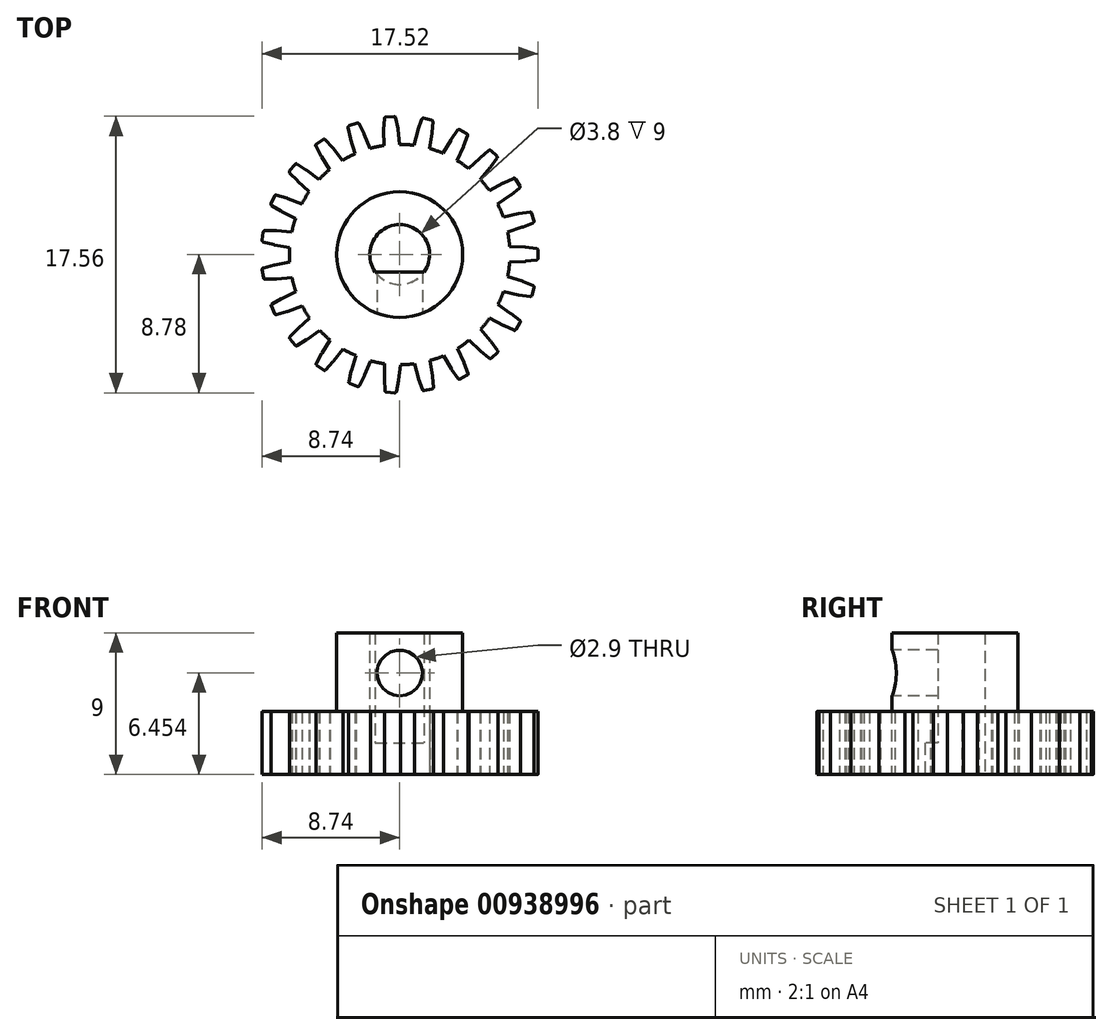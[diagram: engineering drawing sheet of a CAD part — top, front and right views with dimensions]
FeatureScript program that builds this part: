
annotation { "Feature Type Name" : "Feature", "Feature Type Description" : "" }
export const myFeature = defineFeature(function(context is Context, id is Id, definition is map)
    precondition{}
    {
        {
            var Q0;
            Q0=qCreatedBy(makeId("Top.planeOp"),FACE);
            var sketch = newSketch(context, id + "F0", { "sketchPlane" : qUnion([Q0])});
            skArc(sketch, "E0", {"start": v(-1, 6.93) * mm, "mid": v(0.5, -6.98) * mm, "end": v(0, 7) * mm});
            skCircle(sketch, "E1", {"center": v(0, 0) * mm, "radius": 4 * mm});
            skLineSegment(sketch, "E2", {"start": v(-1, 6.93) * mm, "end": v(0, 7) * mm});
            skCircle(sketch, "E3", {"center": v(0, 0) * mm, "radius": 1.9 * mm});
            skLineSegment(sketch, "E4", {"start": v(-0.5, 6.96) * mm, "end": v(-0.57, 7.96) * mm});
            skLineSegment(sketch, "E5", {"start": v(-0.57, 7.96) * mm, "end": v(-1.01, 7.93) * mm});
            skLineSegment(sketch, "E6", {"start": v(-1.01, 7.93) * mm, "end": v(-0.12, 8) * mm});
            skLineSegment(sketch, "E7", {"start": v(-1.01, 7.91) * mm, "end": v(-1, 6.93) * mm});
            skLineSegment(sketch, "E8", {"start": v(-0.11, 7.97) * mm, "end": v(0, 7) * mm});
            skLineSegment(sketch, "E9", {"start": v(-0.57, 7.96) * mm, "end": v(-0.62, 8.76) * mm});
            skLineSegment(sketch, "E10", {"start": v(-0.62, 8.76) * mm, "end": v(-0.88, 8.74) * mm});
            skLineSegment(sketch, "E11", {"start": v(-0.88, 8.74) * mm, "end": v(-0.36, 8.78) * mm});
            skLineSegment(sketch, "E12", {"start": v(-0.97, 8.65) * mm, "end": v(-1.01, 7.95) * mm});
            skLineSegment(sketch, "E13", {"start": v(-0.25, 8.7) * mm, "end": v(-0.12, 8) * mm});
            skPoint(sketch, "E14.visualSharp", {"position": v(-0.27, 8.78) * mm});
            skArc(sketch, "E14.filletArc", {"start": v(-0.25, 8.7) * mm, "mid": v(-0.3, 8.76) * mm, "end": v(-0.36, 8.78) * mm});
            skPoint(sketch, "E15.visualSharp", {"position": v(-0.97, 8.73) * mm});
            skArc(sketch, "E15.filletArc", {"start": v(-0.88, 8.74) * mm, "mid": v(-0.94, 8.71) * mm, "end": v(-0.97, 8.65) * mm});
            skPoint(sketch, "E16.visualSharp", {"position": v(-0.12, 8) * mm});
            skArc(sketch, "E16.filletArc", {"start": v(-0.11, 7.97) * mm, "mid": v(-0.12, 8) * mm, "end": v(-0.12, 8) * mm});
            skPoint(sketch, "E17.visualSharp", {"position": v(-1.01, 7.93) * mm});
            skArc(sketch, "E17.filletArc", {"start": v(-1.01, 7.95) * mm, "mid": v(-1.01, 7.93) * mm, "end": v(-1.01, 7.91) * mm});
            skLineSegment(sketch, "E18", {"start": v(0, 1.9) * mm, "end": v(0, -1.1) * mm, "construction": true});
            skLineSegment(sketch, "E19", {"start": v(-1.55, -1.1) * mm, "end": v(1.55, -1.1) * mm});
            skSolve(sketch);
        }
        {
            var Q0;
            Q0=qCreatedBy(makeId("Front.planeOp"),FACE);
            var sketch = newSketch(context, id + "F1", { "sketchPlane" : qUnion([Q0])});
            skLineSegment(sketch, "E20", {"start": v(0, 0) * mm, "end": v(0, 26.77) * mm, "construction": true});
            skSolve(sketch);
        }
        {
            var Q0;
            Q0=makeQuery(id+"F0.imprint","IMPRINT",FACE,{"disambiguationData":[TD([[makeQuery(id+"F0.imprint","IMPRINT",EDGE,{"derivedFrom":sQuery(id+"F0.wireOp",EDGE,"E1")}),1.0]])]});
            var Q1;
            {var subQ0=sQuery(id+"F0.wireOp",EDGE,"E19");Q1=makeQuery(id+"F0.imprint","IMPRINT",FACE,{"disambiguationData":[TD([[makeQuery(id+"F0.imprint","IMPRINT",EDGE,{"derivedFrom":subQ0}),-1.0]])]});}
            extrude(context, id + "F2", {"entities" : qUnion([Q0, Q1]), "depth" : 7 * mm, "offsetDistance" : 25 * mm});
        }
        {
            var Q0;
            Q0=makeQuery(id+"F0.imprint","IMPRINT",FACE,{"disambiguationData":[TD([[makeQuery(id+"F0.imprint","IMPRINT",EDGE,{"derivedFrom":sQuery(id+"F0.wireOp",EDGE,"E1")}),1.0]])]});
            extrude(context, id + "F3", {"entities" : qUnion([Q0]), "operationType" : NewBodyOperationType.ADD, "oppositeDirection" : true, "depth" : 2 * mm, "offsetDistance" : 25 * mm});
        }
        {
            var Q0;
            Q0=makeQuery(id+"F0.imprint","IMPRINT",FACE,{"disambiguationData":[TD([[makeQuery(id+"F0.imprint","IMPRINT",EDGE,{"derivedFrom":sQuery(id+"F0.wireOp",EDGE,"E1")}),-1.0]])]});
            extrude(context, id + "F4", {"entities" : qUnion([Q0]), "operationType" : NewBodyOperationType.ADD, "depth" : 4 * mm, "offsetDistance" : 25 * mm, "symmetric" : true});
        }
        {
            var Q0;
            Q0=makeQuery(id+"F0.imprint","IMPRINT",FACE,{"disambiguationData":[TD([[makeQuery(id+"F0.imprint","IMPRINT",EDGE,{"derivedFrom":sQuery(id+"F0.wireOp",EDGE,"E2")}),1.0]])]});
            var Q1;
            {var subQ0=sQuery(id+"F0.wireOp",EDGE,"185f444b-8d71-4d4d-b295-205664a3cbeb");Q1=makeQuery(id+"F0.imprint","IMPRINT",FACE,{"disambiguationData":[TD([[makeQuery(id+"F0.imprint","IMPRINT",EDGE,{"derivedFrom":subQ0}),1.0]])]});}
            var Q2;
            {var subQ0=sQuery(id+"F0.wireOp",EDGE,"185f444b-8d71-4d4d-b295-205664a3cbeb");Q2=makeQuery(id+"F0.imprint","IMPRINT",FACE,{"disambiguationData":[TD([[makeQuery(id+"F0.imprint","IMPRINT",EDGE,{"derivedFrom":subQ0}),-1.0]])]});}
            var Q3;
            {var subQ1=sQuery(id+"F0.wireOp",EDGE,"E9");Q3=makeQuery(id+"F0.imprint","IMPRINT",FACE,{"disambiguationData":[TD([[makeQuery(id+"F0.imprint","IMPRINT",EDGE,{"derivedFrom":subQ1}),1.0]])]});}
            var Q4;
            {var subQ1=sQuery(id+"F0.wireOp",EDGE,"E9");Q4=makeQuery(id+"F0.imprint","IMPRINT",FACE,{"disambiguationData":[TD([[makeQuery(id+"F0.imprint","IMPRINT",EDGE,{"derivedFrom":subQ1}),-1.0]])]});}
            extrude(context, id + "F5", {"entities" : qUnion([Q0, Q1, Q2, Q3, Q4]), "depth" : 4 * mm, "offsetDistance" : 25 * mm, "symmetric" : true});
        }
        {
            var Q0;
            Q0=makeQuery(id+"F5.opExtrude","SWEPT_BODY",BODY,{"disambiguationData":[OSD([sQuery(id+"F0.wireOp",EDGE,"E2"),sQuery(id+"F0.wireOp",EDGE,"zY2qvlCe-LwUi-iNXd-wZ7Z-H6Lx6uWpxhC7"),sQuery(id+"F0.wireOp",EDGE,"CL1w9jXF-FcO4-JGJ7-eMMN-SI9SSlm3FFuX")])]});
            var Q1;
            Q1=sQuery(id+"F1.wireOp",EDGE,"E20");
            circularPattern(context, id + "F6", {"operationType" : NewBodyOperationType.ADD, "entities" : qUnion([Q0]), "axis" : qUnion([Q1]), "angle" : 360 * degree, "instanceCount" : 23, "equalSpace" : true});
        }
        {
            var Q0;
            Q0=qCreatedBy(makeId("Front.planeOp"),FACE);
            cPlane(context, id + "F7", {"entities" : qUnion([Q0]), "cplaneType" : CPlaneType.OFFSET, "offset" : 8.8 * mm, "width" : 150 * mm, "height" : 150 * mm});
        }
        {
            var Q0;
            Q0=qCreatedBy(id+"F7.planeOp",FACE);
            var sketch = newSketch(context, id + "F8", { "sketchPlane" : qUnion([Q0])});
            skCircle(sketch, "E21", {"center": v(0, 4.45) * mm, "radius": 1.45 * mm});
            skLineSegment(sketch, "E22", {"start": v(0, 8.41) * mm, "end": v(0, 0.5) * mm});
            skSolve(sketch);
        }
        {
            var Q0;
            {var subQ0=sQuery(id+"F8.wireOp",EDGE,"E22");var subQ1=sQuery(id+"F8.wireOp",EDGE,"E21");var subQ2=makeQuery(id+"F8.imprint","INTERSECT",VERTEX,{"disambiguationData":[OD(0.0)],"derivedFrom":[subQ1,subQ0]});Q0=makeQuery(id+"F8.imprint","IMPRINT",FACE,{"disambiguationData":[TD([[makeQuery(id+"F8.imprint","IMPRINT",EDGE,{"disambiguationData":[TD([[subQ2,1.0]])],"derivedFrom":subQ1}),1.0]])]});}
            var Q1;
            {var subQ0=sQuery(id+"F8.wireOp",EDGE,"E22");var subQ1=sQuery(id+"F8.wireOp",EDGE,"E21");var subQ2=makeQuery(id+"F8.imprint","INTERSECT",VERTEX,{"disambiguationData":[OD(0.0)],"derivedFrom":[subQ1,subQ0]});Q1=makeQuery(id+"F8.imprint","IMPRINT",FACE,{"disambiguationData":[TD([[makeQuery(id+"F8.imprint","IMPRINT",EDGE,{"disambiguationData":[TD([[subQ2,-1.0]])],"derivedFrom":subQ1}),1.0]])]});}
            extrude(context, id + "F9", {"entities" : qUnion([Q0, Q1]), "operationType" : NewBodyOperationType.REMOVE, "oppositeDirection" : true, "depth" : 7.88 * mm, "offsetDistance" : 25 * mm});
        }
    });
